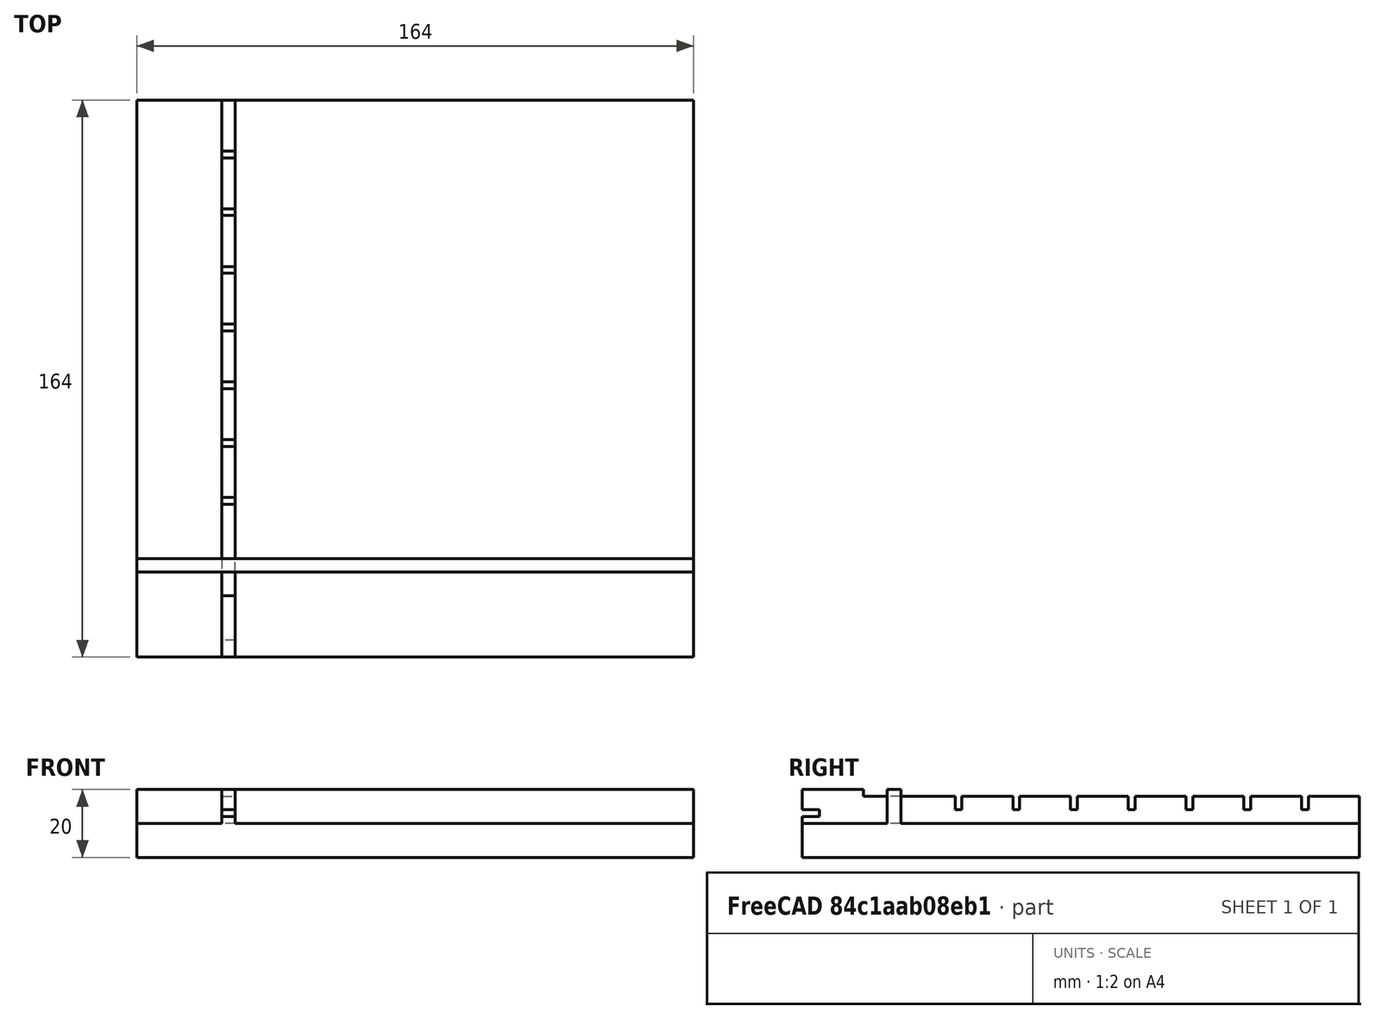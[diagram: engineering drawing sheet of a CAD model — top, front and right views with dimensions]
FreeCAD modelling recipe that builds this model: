
FCSTD DOCUMENT  (FreeCAD 0.21R33771 (Git))
Label: frame_plate_left_bottom
License: All rights reserved
LicenseURL: http://en.wikipedia.org/wiki/All_rights_reserved
objects: Sketcher::SketchObject×6, PartDesign::Pocket×4, PartDesign::Pad×2, PartDesign::LinearPattern×1, PartDesign::Body×1
note: 20 computed .brp shape members not serialized (recipe doc carries the construction recipe); baked Part::Feature solids carry a one-line shape summary decoded from their .brp

FEATURE [Sketcher::SketchObject] Sketch  label="LB-plate"
  FullyConstrained = true
  MapMode = 5
  Support = -> [XY_Plane]
  sketch-geometry (4):
    g0: LineSegment StartX=-82 StartY=82 StartZ=0 EndX=82 EndY=82 EndZ=0
    g1: LineSegment StartX=82 StartY=82 StartZ=0 EndX=82 EndY=-82 EndZ=0
    g2: LineSegment StartX=82 StartY=-82 StartZ=0 EndX=-82 EndY=-82 EndZ=0
    g3: LineSegment StartX=-82 StartY=-82 StartZ=0 EndX=-82 EndY=82 EndZ=0
  constraints (10):
    c: Coincident(g0,g1)
    c: Coincident(g1,g2)
    c: Coincident(g2,g3)
    c: Coincident(g3,g0)
    c: Horizontal(g2)
    c: Vertical(g3)
    c: DistanceX(g2,g1) = 164
    c: DistanceY(g2,g0) = 164
    c: Symmetric(g1,g0,g-1)
    c: Symmetric(g0,g0,g-2)
FEATURE [PartDesign::Pad] Pad
  Direction = (0,0,1)
  Length = 10
  Length2 = 10
  Profile = -> Sketch
  ReferenceAxis = -> Sketch [N_Axis]
  Type = 0
FEATURE [Sketcher::SketchObject] Sketch001  label="LB-bounds"
  FullyConstrained = true
  MapMode = 5
  Placement = pos=(0,0,10) rot=(0,0,1;0rad)
  Support = -> [Pad]
  sketch-geometry (8):
    g0: LineSegment StartX=-82 StartY=-53 StartZ=0 EndX=82 EndY=-53 EndZ=0
    g1: LineSegment StartX=82 StartY=-53 StartZ=0 EndX=82 EndY=-57 EndZ=0
    g2: LineSegment StartX=82 StartY=-57 StartZ=0 EndX=-82 EndY=-57 EndZ=0
    g3: LineSegment StartX=-82 StartY=-57 StartZ=0 EndX=-82 EndY=-53 EndZ=0
    g4: LineSegment StartX=-53 StartY=82 StartZ=0 EndX=-57 EndY=82 EndZ=0
    g5: LineSegment StartX=-57 StartY=82 StartZ=0 EndX=-57 EndY=-82 EndZ=0
    g6: LineSegment StartX=-57 StartY=-82 StartZ=0 EndX=-53 EndY=-82 EndZ=0
    g7: LineSegment StartX=-53 StartY=-82 StartZ=0 EndX=-53 EndY=82 EndZ=0
  constraints (24):
    c: Coincident(g0,g1)
    c: Coincident(g1,g2)
    c: Coincident(g2,g3)
    c: Coincident(g3,g0)
    c: Horizontal(g0)
    c: Horizontal(g2)
    c: Vertical(g1)
    c: Vertical(g3)
    c: DistanceY(g2,g0) = 4
    c: Coincident(g4,g5)
    c: Coincident(g5,g6)
    c: Coincident(g6,g7)
    c: Coincident(g7,g4)
    c: Horizontal(g4)
    c: Horizontal(g6)
    c: Vertical(g5)
    c: Vertical(g7)
    c: DistanceX(g5,g6) = 4
    c: DistanceX(g2,g6) = 29
    c: DistanceY(g5,g0) = 29
    c: DistanceY(g0,g-1) = 53
    c: DistanceX(g6,g-1) = 53
    c: DistanceX(g2,g1) = 164
    c: DistanceY(g5,g4) = 164
FEATURE [PartDesign::Pad] Pad001
  BaseFeature = -> Pad
  Direction = (0,0,1)
  Length = 10
  Length2 = 10
  Profile = -> Sketch001
  ReferenceAxis = -> Sketch001 [N_Axis]
  Type = 0
FEATURE [Sketcher::SketchObject] Sketch002  label="LB-V-plex-cutout"
  ExternalGeometry = -> [Pad001]
  FullyConstrained = true
  MapMode = 5
  Placement = pos=(-53,0,0) rot=(0.57735,0.57735,0.57735;2.0944rad)
  Support = -> [Pad001]
  sketch-geometry (4):
    g0: LineSegment StartX=-64 StartY=20 StartZ=0 EndX=82 EndY=20 EndZ=0
    g1: LineSegment StartX=82 StartY=20 StartZ=0 EndX=82 EndY=18 EndZ=0
    g2: LineSegment StartX=82 StartY=18 StartZ=0 EndX=-64 EndY=18 EndZ=0
    g3: LineSegment StartX=-64 StartY=18 StartZ=0 EndX=-64 EndY=20 EndZ=0
  constraints (12):
    c: Coincident(g0,g1)
    c: Coincident(g1,g2)
    c: Coincident(g2,g3)
    c: Coincident(g3,g0)
    c: Horizontal(g0)
    c: Horizontal(g2)
    c: Vertical(g1)
    c: Vertical(g3)
    c: PointOnObject(g0,g-3)
    c: DistanceX(g-3,g0) = 18
    c: DistanceY(g2,g0) = 2
    c: PointOnObject(g1,g-4)
FEATURE [PartDesign::Pocket] Pocket
  BaseFeature = -> Pad001
  Direction = (-1,0,0)
  Length = 5
  Length2 = 5
  Profile = -> Sketch002
  ReferenceAxis = -> Sketch002 [N_Axis]
  Type = 0
FEATURE [Sketcher::SketchObject] Sketch003  label="LB-H-grid-cutout"
  ExternalGeometry = -> [Pocket]
  FullyConstrained = true
  MapMode = 5
  Placement = pos=(-53,0,0) rot=(0.57735,0.57735,0.57735;2.0944rad)
  Support = -> [Pocket]
  sketch-geometry (4):
    g0: LineSegment StartX=-37 StartY=18 StartZ=0 EndX=-35 EndY=18 EndZ=0
    g1: LineSegment StartX=-35 StartY=18 StartZ=0 EndX=-35 EndY=14 EndZ=0
    g2: LineSegment StartX=-35 StartY=14 StartZ=0 EndX=-37 EndY=14 EndZ=0
    g3: LineSegment StartX=-37 StartY=14 StartZ=0 EndX=-37 EndY=18 EndZ=0
  constraints (12):
    c: Coincident(g0,g1)
    c: Coincident(g1,g2)
    c: Coincident(g2,g3)
    c: Coincident(g3,g0)
    c: Horizontal(g0)
    c: Horizontal(g2)
    c: Vertical(g1)
    c: Vertical(g3)
    c: DistanceX(g0,g0) = 2
    c: DistanceY(g1,g0) = 4
    c: PointOnObject(g0,g-4)
    c: DistanceX(g-3,g2) = 16
FEATURE [PartDesign::Pocket] Pocket001
  BaseFeature = -> Pocket
  Direction = (-1,0,0)
  Length = 5
  Length2 = 5
  Profile = -> Sketch003
  ReferenceAxis = -> Sketch003 [N_Axis]
  Type = 0
FEATURE [PartDesign::LinearPattern] LinearPattern
  BaseFeature = -> Pocket001
  Direction = -> Sketch003 [H_Axis]
  Length = 136
  Occurrences = 9
  Originals = -> [Pocket001]
FEATURE [Sketcher::SketchObject] Sketch004  label="LB-V-cable-cutout"
  ExternalGeometry = -> [LinearPattern]
  FullyConstrained = true
  MapMode = 5
  Placement = pos=(0,0,0) rot=(0.57735,0.57735,0.57735;2.0944rad)
  Support = -> [YZ_Plane]
  sketch-geometry (8):
    g0: LineSegment StartX=-50 StartY=13 StartZ=0 EndX=12.5 EndY=13 EndZ=0
    g1: LineSegment StartX=12.5 StartY=13 StartZ=0 EndX=12.5 EndY=10 EndZ=0
    g2: LineSegment StartX=12.5 StartY=10 StartZ=0 EndX=-50 EndY=10 EndZ=0
    g3: LineSegment StartX=-50 StartY=10 StartZ=0 EndX=-50 EndY=13 EndZ=0
    g4: LineSegment StartX=17.5 StartY=13 StartZ=0 EndX=80 EndY=13 EndZ=0
    g5: LineSegment StartX=80 StartY=13 StartZ=0 EndX=80 EndY=10 EndZ=0
    g6: LineSegment StartX=80 StartY=10 StartZ=0 EndX=17.5 EndY=10 EndZ=0
    g7: LineSegment StartX=17.5 StartY=10 StartZ=0 EndX=17.5 EndY=13 EndZ=0
  constraints (24):
    c: Coincident(g0,g1)
    c: Coincident(g1,g2)
    c: Coincident(g2,g3)
    c: Coincident(g3,g0)
    c: Horizontal(g0)
    c: Horizontal(g2)
    c: Vertical(g1)
    c: Vertical(g3)
    c: Coincident(g4,g5)
    c: Coincident(g5,g6)
    c: Coincident(g6,g7)
    c: Coincident(g7,g4)
    c: Horizontal(g4)
    c: Horizontal(g6)
    c: Vertical(g5)
    c: Vertical(g7)
    c: DistanceY(g1,g0) = 3
    c: DistanceY(g6,g4) = 3
    c: DistanceX(g0,g4) = 5
    c: DistanceX(g-3,g0) = 3
    c: PointOnObject(g2,g-4)
    c: PointOnObject(g6,g-4)
    c: DistanceX(g0,g-5) = 1.5
    c: DistanceX(g4,g-6) = 2
FEATURE [PartDesign::Pocket] Pocket002
  BaseFeature = -> LinearPattern
  Direction = (-1,2e-16,-3e-16)
  Length = 5
  Length2 = 5
  Profile = -> Sketch004
  ReferenceAxis = -> Sketch004 [N_Axis]
  Type = 0
FEATURE [Sketcher::SketchObject] Sketch005  label="LB-H-plex-cutout"
  ExternalGeometry = -> [Pocket002]
  FullyConstrained = true
  MapMode = 5
  Placement = pos=(0,-82,0) rot=(1,0,0;1.5708rad)
  Support = -> [Pocket002]
  sketch-geometry (4):
    g0: LineSegment StartX=-57 StartY=14 StartZ=0 EndX=64 EndY=14 EndZ=0
    g1: LineSegment StartX=64 StartY=14 StartZ=0 EndX=64 EndY=12 EndZ=0
    g2: LineSegment StartX=64 StartY=12 StartZ=0 EndX=-57 EndY=12 EndZ=0
    g3: LineSegment StartX=-57 StartY=12 StartZ=0 EndX=-57 EndY=14 EndZ=0
  constraints (11):
    c: Coincident(g0,g1)
    c: Coincident(g1,g2)
    c: Coincident(g2,g3)
    c: Coincident(g3,g0)
    c: Horizontal(g0)
    c: Horizontal(g2)
    c: Vertical(g1)
    c: Vertical(g3)
    c: DistanceX(g0,g-3) = 18
    c: DistanceY(g1,g0) = 2
    c: Coincident(g0,g-4)
FEATURE [PartDesign::Pocket] Pocket003
  BaseFeature = -> Pocket002
  Direction = (0,1,-2e-16)
  Length = 5
  Length2 = 5
  Profile = -> Sketch005
  ReferenceAxis = -> Sketch005 [N_Axis]
  Type = 0
FEATURE [PartDesign::Body] Body  label="LB_plate"
  Group = -> [Sketch,Pad,Sketch001,Pad001,Sketch002,Pocket,Sketch003,Pocket001,LinearPattern,Sketch004,Pocket002,Sketch005,Pocket003]
  Origin = -> Origin
  Tip = -> Pocket003
